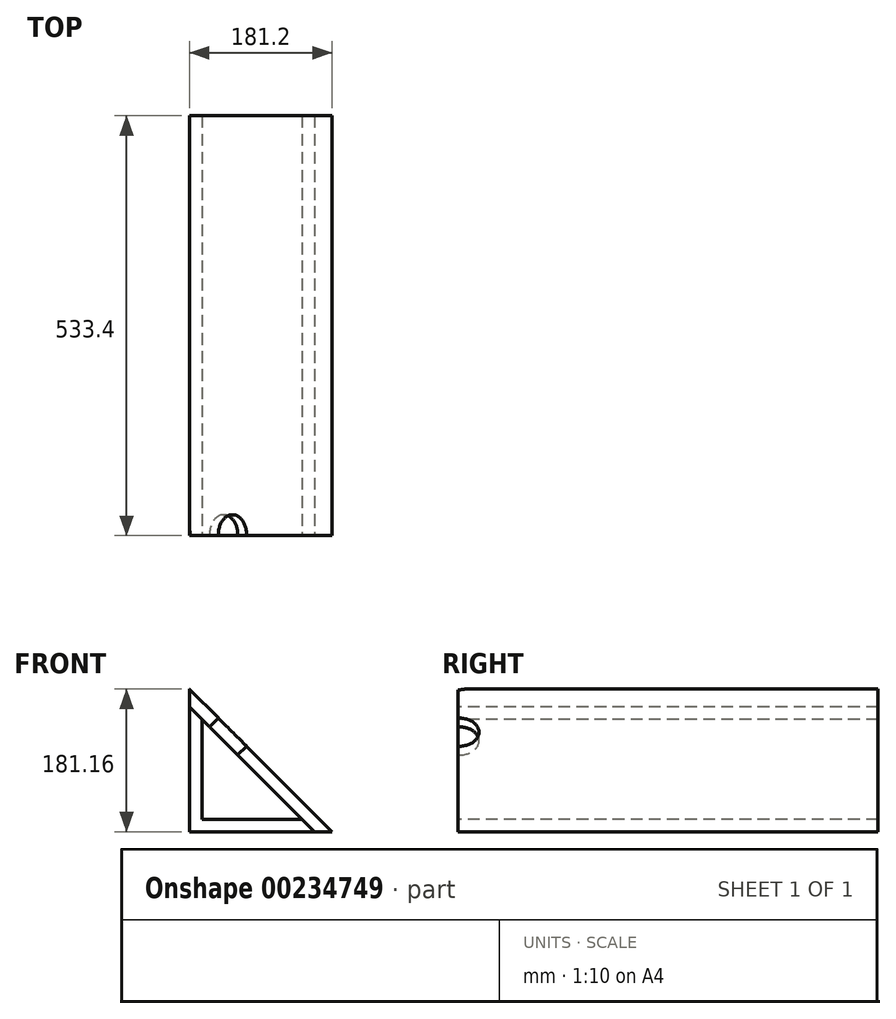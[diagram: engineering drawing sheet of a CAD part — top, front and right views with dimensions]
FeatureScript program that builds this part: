
annotation { "Feature Type Name" : "Feature", "Feature Type Description" : "" }
export const myFeature = defineFeature(function(context is Context, id is Id, definition is map)
    precondition{}
    {
        {
            var Q0;
            Q0=qCreatedBy(makeId("Front.planeOp"),FACE);
            var sketch = newSketch(context, id + "F0", { "sketchPlane" : qUnion([Q0])});
            skLineSegment(sketch, "E0", {"start": v(0, 0) * mm, "end": v(158.75, 0) * mm});
            skLineSegment(sketch, "E1", {"start": v(158.75, 0) * mm, "end": v(142.87, 15.88) * mm});
            skLineSegment(sketch, "E2", {"start": v(142.87, 15.88) * mm, "end": v(15.88, 15.87) * mm});
            skLineSegment(sketch, "E3", {"start": v(15.88, 15.87) * mm, "end": v(15.88, 142.88) * mm});
            skLineSegment(sketch, "E4", {"start": v(15.88, 142.88) * mm, "end": v(0, 158.75) * mm});
            skLineSegment(sketch, "E5", {"start": v(0, 158.75) * mm, "end": v(0, 0) * mm});
            skLineSegment(sketch, "E6", {"start": v(158.75, 0) * mm, "end": v(0, 158.7) * mm});
            skLineSegment(sketch, "E7.0", {"start": v(181.2, 0) * mm, "end": v(0, 181.16) * mm});
            skLineSegment(sketch, "E8", {"start": v(0, 158.75) * mm, "end": v(0, 181.16) * mm});
            skLineSegment(sketch, "E9", {"start": v(158.75, 0) * mm, "end": v(181.2, 0) * mm});
            skLineSegment(sketch, "E10", {"start": v(62.2, 96.52) * mm, "end": v(30.78, 65.09) * mm, "construction": true});
            skLineSegment(sketch, "E11", {"start": v(30.78, 65.09) * mm, "end": v(66.7, 29.17) * mm, "construction": true});
            skLineSegment(sketch, "E12", {"start": v(66.7, 29.17) * mm, "end": v(98.13, 60.6) * mm, "construction": true});
            skLineSegment(sketch, "E13", {"start": v(98.13, 60.6) * mm, "end": v(109.35, 71.83) * mm, "construction": true});
            skSolve(sketch);
        }
        {
            var Q0;
            Q0=makeQuery(id+"F0.imprint","IMPRINT",FACE,{"disambiguationData":[TD([[makeQuery(id+"F0.imprint","IMPRINT",EDGE,{"derivedFrom":sQuery(id+"F0.wireOp",EDGE,"quRk46w5-69zu-gnJ7-eGTH-7Ixriuc6cQiM")}),-1.0]])]});
            var Q1;
            {var subQ6=sQuery(id+"F0.wireOp",EDGE,"E0");Q1=makeQuery(id+"F0.imprint","IMPRINT",FACE,{"disambiguationData":[TD([[makeQuery(id+"F0.imprint","IMPRINT",EDGE,{"derivedFrom":subQ6}),1.0]])]});}
            var Q2;
            {var subQ5=sQuery(id+"F0.wireOp",EDGE,"E1");Q2=makeQuery(id+"F0.imprint","IMPRINT",FACE,{"disambiguationData":[TD([[makeQuery(id+"F0.imprint","IMPRINT",EDGE,{"derivedFrom":subQ5}),-1.0]])]});}
            extrude(context, id + "F1", {"entities" : qUnion([Q0, Q1, Q2]), "oppositeDirection" : true, "depth" : 533.4 * mm});
        }
        {
            var Q0;
            Q0=makeQuery(id+"F1.opExtrude","SWEPT_FACE",FACE,{"disambiguationData":[OSD([sQuery(id+"F0.wireOp",EDGE,"E7.0")])]});
            var sketch = newSketch(context, id + "F2", { "sketchPlane" : qUnion([Q0])});
            skSolve(sketch);
        }
        {
            var Q0;
            {var subQ0=sQuery(id+"F0.wireOp",EDGE,"E7.0");Q0=makeQuery(id+"F2.imprint","IMPRINT",FACE,{"disambiguationData":[TD([[makeQuery(id+"F2.imprint","IMPRINT",EDGE,{"derivedFrom":makeQuery(id+"F1.opExtrude","CAP_EDGE",EDGE,{"disambiguationData":[OSD([subQ0])],"isStart":true})}),-1.0]])]});}
            var sketch = newSketch(context, id + "F3", { "sketchPlane" : qUnion([Q0])});
            skLineSegment(sketch, "E14", {"start": v(1.15, 0) * mm, "end": v(1.15, 407.59) * mm, "construction": true});
            skCircle(sketch, "E15", {"center": v(1.15, 50.8) * mm, "radius": 25.4 * mm});
            skCircle(sketch, "E16", {"center": v(1.15, 152.4) * mm, "radius": 25.4 * mm});
            skCircle(sketch, "E17", {"center": v(1.15, 254) * mm, "radius": 25.4 * mm});
            skCircle(sketch, "E18", {"center": v(1.15, 355.6) * mm, "radius": 25.4 * mm});
            skLineSegment(sketch, "E19.bottom", {"start": v(-76.2, 403.23) * mm, "end": v(76.2, 403.23) * mm});
            skLineSegment(sketch, "E19.top", {"start": v(-76.2, 517.53) * mm, "end": v(76.2, 517.53) * mm});
            skLineSegment(sketch, "E19.left", {"start": v(-76.2, 403.23) * mm, "end": v(-76.2, 517.53) * mm});
            skLineSegment(sketch, "E19.right", {"start": v(76.2, 403.23) * mm, "end": v(76.2, 517.53) * mm});
            skPoint(sketch, "E19.middle", {"position": v(0, 460.38) * mm});
            skSolve(sketch);
        }
        {
            var Q0;
            Q0 = qSketchRegion(id + "F3", true);
            extrude(context, id + "F4", {"entities" : qUnion([Q0]), "operationType" : NewBodyOperationType.REMOVE, "oppositeDirection" : true, "depth" : 17.78 * mm});
        }
    });
